# Revit family: F115-41.5x18x18
name_source: partatom
category: Furniture Systems
units: mm (PartAtom-declared; Revit-internal decimal feet)

## family parameters
Always vertical = Yes
Cut with Voids When Loaded = No
Part Type = Normal
Room Calculation Point = No
Round Connector Dimension = Use Diameter
Shared = No
Work Plane-Based = No

## types (14) — shared parameters
3" Rectangle Leg = <By Category>
6" Rectangle Leg = <By Category>
Base = <By Category>
Description = Network Series - Trapezoid Bench (Seat height 18")
Glide = <By Category>
Laminate Top = <By Category>
Low Profile = Black
Manufacturer = FOMCORE
Mod Leg = <By Category>
Model = F115-41.5x18x18
Seat Fabric = <By Category>
Side Fabric = <By Category>
Triangle Leg = <By Category>
URL = https://fomcore.com

## per-type parameters (varying)
| type | C3 | G1 | L- TOP | L1 | LEG OPTIONS | Leg H | M6 | R3 | R6 | Seat H | T6 |
| F115-41.5x18x18-G1 | No | Yes | No | No | 1 | 0' - 1 1/2" | No | No | No | 1' - 6" | No |
| F115-41.5x18x18-G1-TFL | No | Yes | Yes | No | 1 | 0' - 1 1/2" | No | No | No | 1' - 5 1/4" | No |
| F115-41.5x18x18-L1 | No | No | No | Yes | 2 | 0' - 1 1/2" | No | No | No | 1' - 6" | No |
| F115-41.5x18x18-L1-TFL | No | No | Yes | Yes | 2 | 0' - 1 1/2" | No | No | No | 1' - 5 1/4" | No |
| F115-41.5x18x18-M6 | No | No | Yes | No | 4 | 0' - 6 1/2" | Yes | No | No | 1' - 6" | No |
| F115-41.5x18x18-M6-TFL | No | No | Yes | No | 4 | 0' - 6 1/2" | Yes | No | No | 1' - 5 1/4" | No |
| F115-41.5x18x18-C3 | Yes | No | No | No | 3 | 0' - 3 1/2" | No | No | No | 1' - 6" | No |
| F115-41.5x18x18-C3-TFL | Yes | No | Yes | No | 3 | 0' - 3 1/2" | No | No | No | 1' - 5 1/4" | No |
| F115-41.5x18x18-R3 | No | No | No | No | 5 | 0' - 3 1/2" | No | Yes | No | 1' - 6" | No |
| F115-41.5x18x18-R3-TFL | No | No | Yes | No | 5 | 0' - 3 1/2" | No | Yes | No | 1' - 5 1/4" | No |
| F115-41.5x18x18-R6-TFL | No | No | Yes | No | 6 | 0' - 6 1/2" | No | No | Yes | 1' - 5 1/4" | No |
| F115-41.5x18x18-R6 | No | No | No | No | 6 | 0' - 6 1/2" | No | No | Yes | 1' - 6" | No |
| F115-41.5x18x18-T6 | No | No | No | No | 7 | 0' - 6 1/2" | No | No | No | 1' - 6" | Yes |
| F115-41.5x18x18-T6-TFL | No | No | Yes | No | 7 | 0' - 6 1/2" | No | No | No | 1' - 5 1/4" | Yes |

## geometry (parser evidence)
native form markers: Sweep x1
no freeform markers — native parametric forms only
